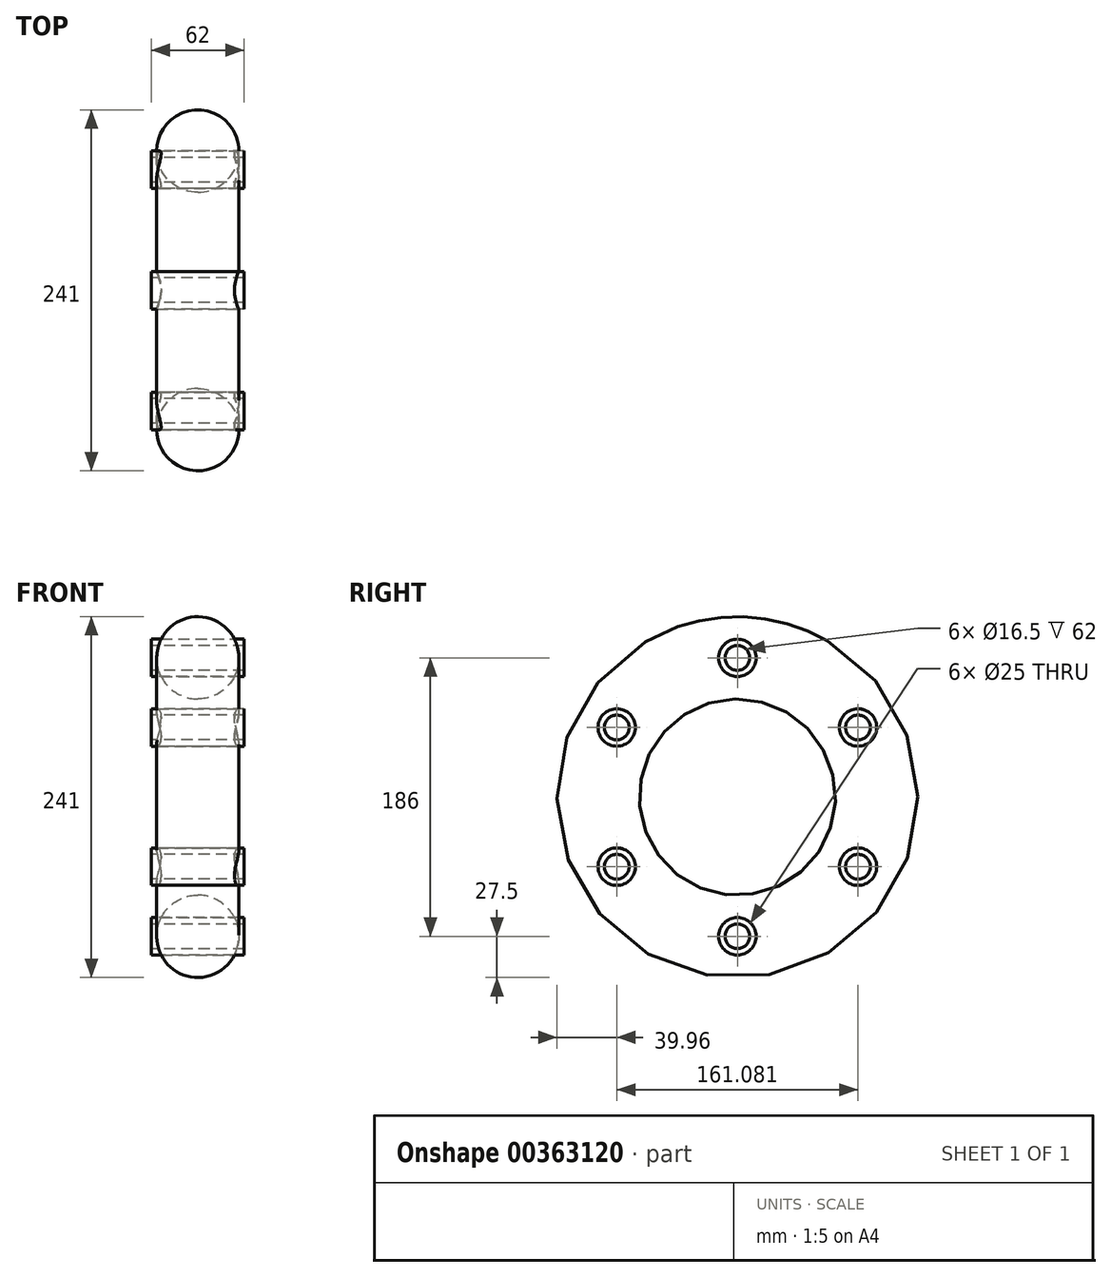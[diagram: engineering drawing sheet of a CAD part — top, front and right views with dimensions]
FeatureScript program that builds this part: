
annotation { "Feature Type Name" : "Feature", "Feature Type Description" : "" }
export const myFeature = defineFeature(function(context is Context, id is Id, definition is map)
    precondition{}
    {
        {
            var Q0;
            Q0=qCreatedBy(makeId("Front.planeOp"),FACE);
            var sketch = newSketch(context, id + "F0", { "sketchPlane" : qUnion([Q0])});
            skLineSegment(sketch, "E0", {"start": v(-171.45, 0) * mm, "end": v(178.4, 0) * mm, "construction": true});
            skCircle(sketch, "E1", {"center": v(0, 93) * mm, "radius": 27.5 * mm});
            skSolve(sketch);
        }
        {
            var Q0;
            Q0=makeQuery(id+"F0.imprint","IMPRINT",FACE,{"disambiguationData":[TD([[makeQuery(id+"F0.imprint","IMPRINT",EDGE,{"derivedFrom":sQuery(id+"F0.wireOp",EDGE,"E1")}),1.0]])]});
            var Q1;
            Q1=sQuery(id+"F0.wireOp",EDGE,"E0");
            revolve(context, id + "F1", {"entities" : qUnion([Q0]), "axis" : qUnion([Q1]), "revolveType" : RevolveType.FULL});
        }
        {
            var Q0;
            Q0=qCreatedBy(makeId("Right.planeOp"),FACE);
            var sketch = newSketch(context, id + "F2", { "sketchPlane" : qUnion([Q0])});
            skCircle(sketch, "E2", {"center": v(0, 93) * mm, "radius": 12.5 * mm});
            skCircle(sketch, "E3.1.0", {"center": v(-80.54, 46.5) * mm, "radius": 12.5 * mm});
            skCircle(sketch, "E3.2.0", {"center": v(-80.54, -46.5) * mm, "radius": 12.5 * mm});
            skPoint(sketch, "E3.center", {"position": v(0, 0) * mm});
            skCircle(sketch, "E4.1.3.0", {"center": v(0, -93) * mm, "radius": 12.5 * mm});
            skCircle(sketch, "E4.1.4.0", {"center": v(80.54, -46.5) * mm, "radius": 12.5 * mm});
            skCircle(sketch, "E4.1.5.0", {"center": v(80.54, 46.5) * mm, "radius": 12.5 * mm});
            skSolve(sketch);
        }
        {
            var Q0;
            Q0 = qSketchRegion(id + "F2", true);
            extrude(context, id + "F3", {"entities" : qUnion([Q0]), "operationType" : NewBodyOperationType.REMOVE, "endBound" : BoundingType.THROUGH_ALL, "oppositeDirection" : true, "depth" : 25 * mm, "hasSecondDirection" : true, "secondDirectionBound" : SecondDirectionBoundingType.THROUGH_ALL, "secondDirectionOppositeDirection" : false, "secondDirectionDepth" : 25 * mm});
        }
        {
            var Q0;
            Q0=qCreatedBy(makeId("Right.planeOp"),FACE);
            var sketch = newSketch(context, id + "F4", { "sketchPlane" : qUnion([Q0])});
            skCircle(sketch, "E5", {"center": v(0, 93) * mm, "radius": 8.25 * mm});
            skCircle(sketch, "E6", {"center": v(0, 93) * mm, "radius": 12.5 * mm});
            skCircle(sketch, "E7.1.0", {"center": v(-80.54, 46.5) * mm, "radius": 12.5 * mm});
            skCircle(sketch, "E7.1.1", {"center": v(-80.54, 46.5) * mm, "radius": 8.25 * mm});
            skCircle(sketch, "E7.2.0", {"center": v(-80.54, -46.5) * mm, "radius": 12.5 * mm});
            skCircle(sketch, "E7.2.1", {"center": v(-80.54, -46.5) * mm, "radius": 8.25 * mm});
            skPoint(sketch, "E7.center", {"position": v(0, 0) * mm});
            skCircle(sketch, "E8.1.3.0", {"center": v(0, -93) * mm, "radius": 12.5 * mm});
            skCircle(sketch, "E8.2.3.0", {"center": v(0, -93) * mm, "radius": 8.25 * mm});
            skCircle(sketch, "E8.1.4.0", {"center": v(80.54, -46.5) * mm, "radius": 12.5 * mm});
            skCircle(sketch, "E8.2.4.0", {"center": v(80.54, -46.5) * mm, "radius": 8.25 * mm});
            skCircle(sketch, "E8.1.5.0", {"center": v(80.54, 46.5) * mm, "radius": 12.5 * mm});
            skCircle(sketch, "E8.2.5.0", {"center": v(80.54, 46.5) * mm, "radius": 8.25 * mm});
            skSolve(sketch);
        }
        {
            var Q0;
            Q0 = qSketchRegion(id + "F4", true);
            extrude(context, id + "F5", {"entities" : qUnion([Q0]), "depth" : 31 * mm, "hasSecondDirection" : true, "secondDirectionOppositeDirection" : true, "secondDirectionDepth" : 31 * mm});
        }
    });
